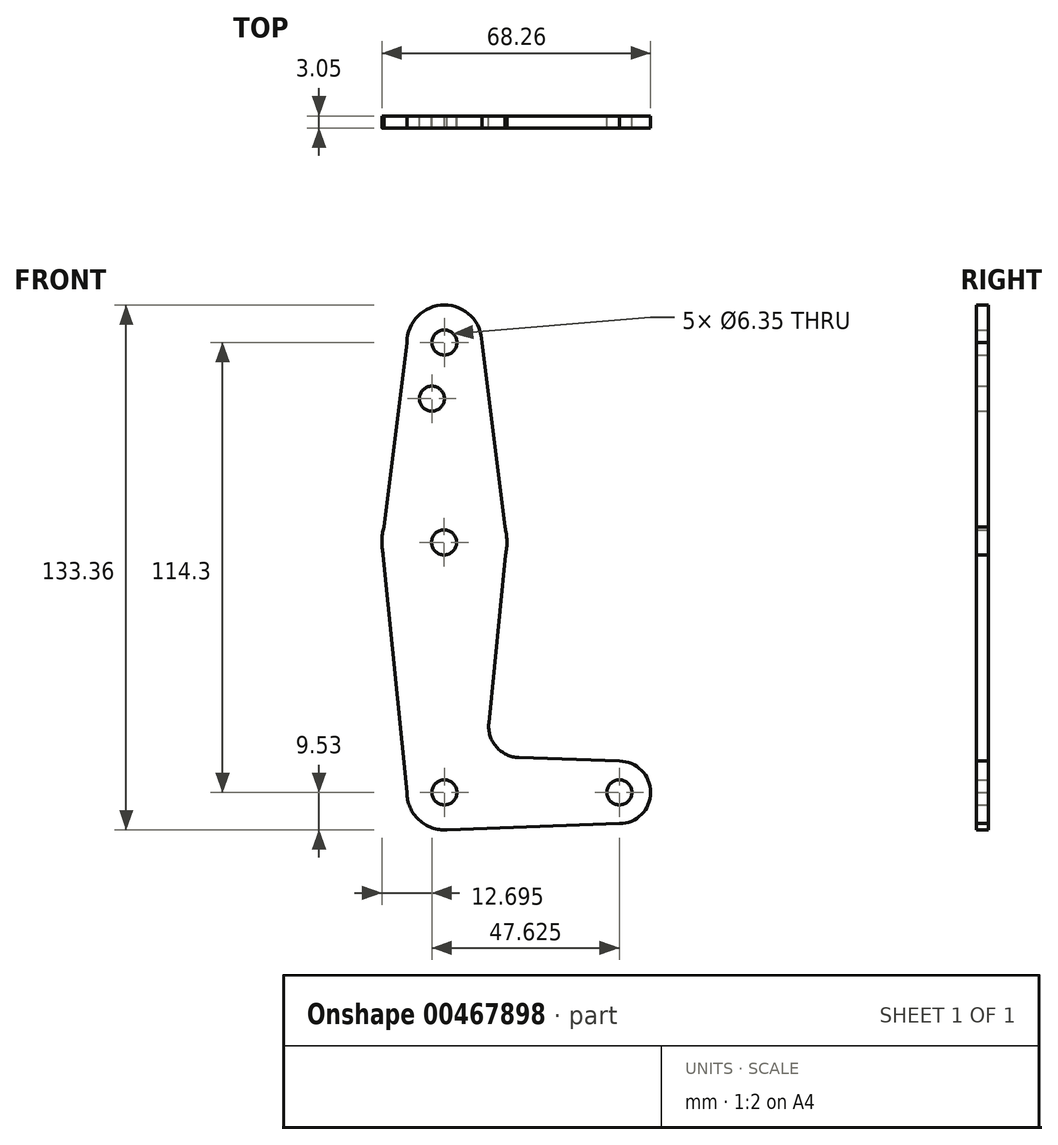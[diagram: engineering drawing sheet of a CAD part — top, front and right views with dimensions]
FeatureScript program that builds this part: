
annotation { "Feature Type Name" : "Feature", "Feature Type Description" : "" }
export const myFeature = defineFeature(function(context is Context, id is Id, definition is map)
    precondition{}
    {
        {
            var Q0;
            Q0=qCreatedBy(makeId("Front.planeOp"),FACE);
            var sketch = newSketch(context, id + "F0", { "sketchPlane" : qUnion([Q0])});
            skCircle(sketch, "E0", {"center": v(0, 0) * mm, "radius": 9.53 * mm});
            skLineSegment(sketch, "E1", {"start": v(0, 0) * mm, "end": v(0, 114.3) * mm});
            skCircle(sketch, "E2", {"center": v(0, 63.5) * mm, "radius": 15.88 * mm});
            skCircle(sketch, "E3", {"center": v(0, 114.3) * mm, "radius": 9.53 * mm});
            skLineSegment(sketch, "E4", {"start": v(0, 0) * mm, "end": v(44.45, 0) * mm});
            skCircle(sketch, "E5", {"center": v(44.45, 0) * mm, "radius": 7.94 * mm});
            skLineSegment(sketch, "E6", {"start": v(-9.52, 114.3) * mm, "end": v(-15.88, 63.5) * mm});
            skLineSegment(sketch, "E7", {"start": v(11.28, 17.59) * mm, "end": v(15.88, 63.5) * mm});
            skLineSegment(sketch, "E8", {"start": v(15.88, 63.5) * mm, "end": v(9.52, 114.3) * mm});
            skLineSegment(sketch, "E9", {"start": v(44.45, 7.94) * mm, "end": v(18.91, 8.85) * mm});
            skLineSegment(sketch, "E10", {"start": v(0, -9.53) * mm, "end": v(44.45, -7.94) * mm});
            skCircle(sketch, "E11", {"center": v(0, 114.3) * mm, "radius": 3.18 * mm});
            skCircle(sketch, "E12", {"center": v(-3.18, 100.03) * mm, "radius": 3.18 * mm});
            skCircle(sketch, "E13", {"center": v(-0.09, 63.53) * mm, "radius": 3.18 * mm});
            skCircle(sketch, "E14", {"center": v(0, 0) * mm, "radius": 3.18 * mm});
            skCircle(sketch, "E15", {"center": v(44.45, 0) * mm, "radius": 3.18 * mm});
            skArc(sketch, "E16.filletArc", {"start": v(11.28, 17.59) * mm, "mid": v(13.2, 11.57) * mm, "end": v(18.91, 8.85) * mm});
            skLineSegment(sketch, "E17", {"start": v(-15.88, 63.5) * mm, "end": v(-9.52, 0) * mm});
            skSolve(sketch);
        }
        {
            var Q0;
            Q0=qSketchRegion(id+"F0",true);
            var Q1;
            {var subQ0=sQuery(id+"F0.wireOp",EDGE,"E1");var subQ1=sQuery(id+"F0.wireOp",EDGE,"E0");var subQ2=makeQuery(id+"F0.imprint","INTERSECT",VERTEX,{"derivedFrom":[subQ1,subQ0]});Q1=makeQuery(id+"F0.imprint","IMPRINT",FACE,{"disambiguationData":[TD([[makeQuery(id+"F0.imprint","IMPRINT",EDGE,{"disambiguationData":[TD([[subQ2,1.0]])],"derivedFrom":subQ1}),1.0]])]});}
            extrude(context, id + "F1", {"entities" : qUnion([Q0, Q1]), "depth" : 3.05 * mm});
        }
    });
